# Revit family: Faucet-Lavatory-Grohe-Lineare-20578_Series
name_source: partatom
category: Plumbing Fixtures
revit_build: Autodesk Revit 2014 (Build: 20130308_1515(x64)
units: mm (PartAtom-declared; Revit-internal decimal feet)

## types (2) — shared parameters
ADA Compliant = Yes
Assembly Code = D2020300
CW Connection = Yes
CWFU = 1.5
CalGreen Compliant = Yes
Cold Water Connection Diameter = 3/8"
Cold Water Connection Radius = 3/16"
Default Elevation = 0"
Description = Lineare 8" Widespread Two-Handle Bathroom Faucet M-Size
HW Connection = Yes
HWFU = 1.5
Height = 4 3/4"
Hot Water Connection Diameter = 0"
Hot Water Connection Radius = 3/16"
Installation Type = Deck-Mounted
Length = 5"
Manufacturer = Grohe
Price = Prices may vary. Please consult Manufacturer Representative for most up-to-date price list.
Product Page URL = https://www.grohe.us
Shipping Weight = 0.00 lb
URL = https://www.grohe.com
Vent Connection = No
WFU = 2
Warranty Documentation Link = https://cdn.cloud.grohe.com
Waste Connection = No
Width = 10"
cUPC Compliant = Yes

## per-type parameters (varying)
| type | Faucet Handle Type | Finish | Material |
| 2057800A | 20578 Faucet Handle : 20578 Faucet Handle 00A | Metal-Grohe-00A-Chrome | Metal-Grohe-00A-Chrome |
| 20578ENA | 20578 Faucet Handle : 20578 Faucet Handle ENA | Metal-Grohe-ENA-Brushed Nickel | Metal-Grohe-ENA-Brushed Nickel |

note: column(s) folded — value = type name in every type: Model

## geometry (parser evidence)
native form markers: Sweep x1
no freeform markers — native parametric forms only
